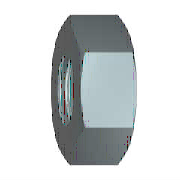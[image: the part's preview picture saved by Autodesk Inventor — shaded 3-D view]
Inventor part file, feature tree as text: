
AUTODESK INVENTOR PART (.ipt)
format: ipt  version: 2023.1 (Build 271208000, 208)  size: 163,328 bytes
history: native  units: mm (DEFAULTED — no unit token found)
features: sketch x3, chamfer x1, hole x1, other x1, plane x1
ambient origin geometry x7: Origin, YZ Plane, XZ Plane, X Axis, Y Axis, Z Axis, Center Point
bodies: Solid1 (feature_tree), Body (feature_tree)
feature tree (7):
  chamfer  "Chamfer1"  Angle=30.0deg  [1 undecoded]
  hole  "Thread"  [1 undecoded]
  other  "Work Axis1"
  plane  "Work Plane1"
  sketch  "Sketch1"  dims[d0=31.176915mm]
  sketch  "Sketch2"  dims[d1=17.6mm]
  sketch  "Sketch3"  dims[d2=0.0mm d3=30.0deg d4=30.0deg d5=24.85mm d6=24.85mm d7=90.0deg d25=16.376mm d26=6.0mm d27=4.0mm d28=2.0mm d29=14.3117mm d30=8.0mm d31=20.594885mm d8=0.811899mm d9=30.0deg d10=0.811899mm d11=30.0deg d13=0.0mm d14=0.0mm d39=0.0mm d40=0.811899mm d41=0.811899mm d42=0.0mm]
note: 2 required parameter values undecoded (feature->parameter linkage not recoverable at this tier; creation-order binding heuristic only, values carry confidence <= 0.55)
